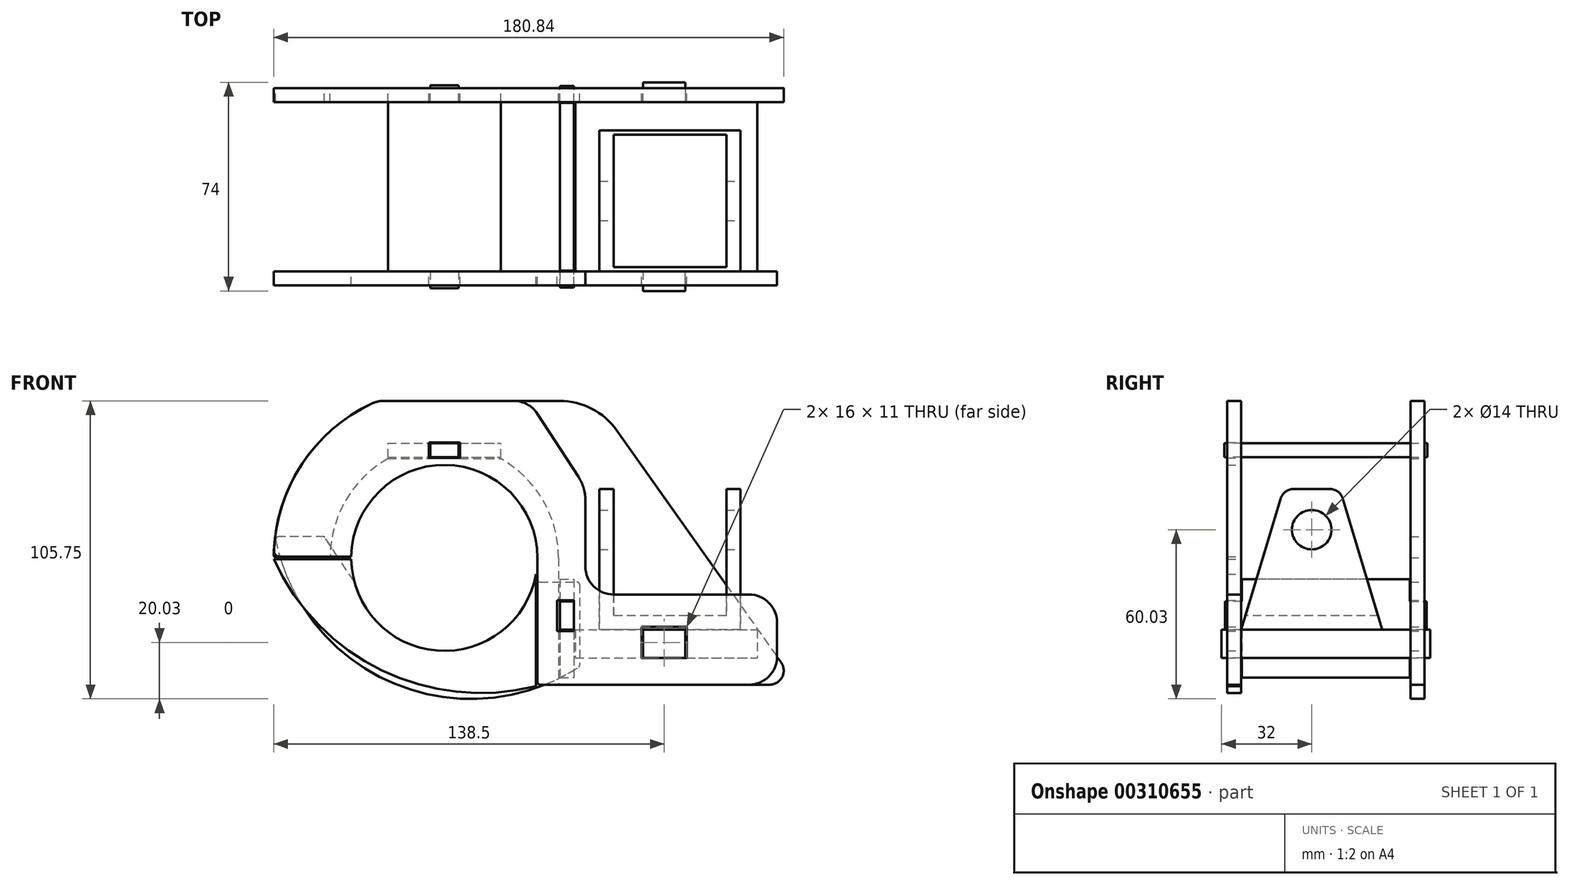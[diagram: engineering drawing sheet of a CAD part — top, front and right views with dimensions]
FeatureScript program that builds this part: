
annotation { "Feature Type Name" : "Feature", "Feature Type Description" : "" }
export const myFeature = defineFeature(function(context is Context, id is Id, definition is map)
    precondition{}
    {
        {
            var Q0;
            Q0=qCreatedBy(makeId("Front.planeOp"),FACE);
            var sketch = newSketch(context, id + "F0", { "sketchPlane" : qUnion([Q0])});
            skArc(sketch, "E0", {"start": v(40.5, 0) * mm, "mid": v(0, 40.5) * mm, "end": v(-40.5, 0) * mm, "construction": true});
            skLineSegment(sketch, "E1", {"start": v(-20, 35.22) * mm, "end": v(-5.5, 35.22) * mm});
            skLineSegment(sketch, "E2", {"start": v(-5.5, 35.22) * mm, "end": v(-5.5, 40.72) * mm});
            skLineSegment(sketch, "E3", {"start": v(-5.5, 40.72) * mm, "end": v(5.5, 40.72) * mm});
            skLineSegment(sketch, "E4", {"start": v(5.5, 40.72) * mm, "end": v(5.5, 35.22) * mm});
            skLineSegment(sketch, "E5", {"start": v(5.5, 35.22) * mm, "end": v(20, 35.22) * mm});
            skPoint(sketch, "E6", {"position": v(0, 40.72) * mm});
            skArc(sketch, "E7", {"start": v(-20, 35.22) * mm, "mid": v(-35, 20.37) * mm, "end": v(-40.5, 0) * mm});
            skArc(sketch, "E8", {"start": v(40.5, 0) * mm, "mid": v(35, 20.37) * mm, "end": v(20, 35.22) * mm});
            skArc(sketch, "E9.0", {"start": v(-25.7, 54.77) * mm, "mid": v(-50.79, 32.87) * mm, "end": v(-60.5, 1.02) * mm});
            skLineSegment(sketch, "E10", {"start": v(-59.5, 0) * mm, "end": v(-40.5, 0) * mm});
            skLineSegment(sketch, "E11", {"start": v(-21.45, 55.72) * mm, "end": v(40.81, 55.72) * mm});
            skLineSegment(sketch, "E12", {"start": v(40.5, 0) * mm, "end": v(40.5, -15) * mm});
            skLineSegment(sketch, "E13", {"start": v(40.5, -45) * mm, "end": v(115.34, -45) * mm});
            skArc(sketch, "E14", {"start": v(-32.5, 0) * mm, "mid": v(0, -32.5) * mm, "end": v(32.5, 0) * mm, "construction": true});
            skLineSegment(sketch, "E15", {"start": v(-40.5, 0) * mm, "end": v(-32.5, 0) * mm, "construction": true});
            skLineSegment(sketch, "E16", {"start": v(40.5, 0) * mm, "end": v(32.5, 0) * mm, "construction": true});
            skPoint(sketch, "E17", {"position": v(80, 10) * mm});
            skLineSegment(sketch, "E18", {"start": v(61.22, 45.15) * mm, "end": v(119.42, -37.11) * mm});
            skLineSegment(sketch, "E19.bottom", {"start": v(70, -24.5) * mm, "end": v(86, -24.5) * mm});
            skLineSegment(sketch, "E19.top", {"start": v(70, -35.5) * mm, "end": v(86, -35.5) * mm});
            skLineSegment(sketch, "E19.left", {"start": v(70, -24.5) * mm, "end": v(70, -35.5) * mm});
            skLineSegment(sketch, "E19.right", {"start": v(86, -24.5) * mm, "end": v(86, -35.5) * mm});
            skPoint(sketch, "E20.visualSharp", {"position": v(-23.58, 55.72) * mm});
            skArc(sketch, "E20.filletArc", {"start": v(-21.45, 55.72) * mm, "mid": v(-23.63, 55.48) * mm, "end": v(-25.7, 54.77) * mm});
            skPoint(sketch, "E21.visualSharp", {"position": v(53.75, 55.72) * mm});
            skArc(sketch, "E21.filletArc", {"start": v(61.22, 45.15) * mm, "mid": v(52.3, 52.92) * mm, "end": v(40.81, 55.72) * mm});
            skPoint(sketch, "E22.visualSharp", {"position": v(125, -45) * mm});
            skArc(sketch, "E22.filletArc", {"start": v(115.34, -45) * mm, "mid": v(119.78, -42.3) * mm, "end": v(119.42, -37.11) * mm});
            skLineSegment(sketch, "E23", {"start": v(40.5, -15) * mm, "end": v(46, -15) * mm});
            skLineSegment(sketch, "E24", {"start": v(46, -15) * mm, "end": v(46, -26) * mm});
            skLineSegment(sketch, "E25", {"start": v(46, -26) * mm, "end": v(40.5, -26) * mm});
            skLineSegment(sketch, "E26.trimOffspring", {"start": v(40.5, -26) * mm, "end": v(40.5, -45) * mm});
            skPoint(sketch, "E27.visualSharp", {"position": v(-60.5, 0) * mm});
            skArc(sketch, "E27.filletArc", {"start": v(-60.5, 1.02) * mm, "mid": v(-60.2, 0.3) * mm, "end": v(-59.5, 0) * mm});
            skSolve(sketch);
        }
        {
            var Q0;
            Q0 = qSketchRegion(id + "F0", true);
            var Q1;
            Q1 = qConstructionFilter(qBodyType(qCreatedBy(id + "F0" ,EDGE), BodyType.WIRE), ConstructionObject.NO);
            extrude(context, id + "F1", {"entities" : qUnion([Q0]), "surfaceEntities" : qUnion([Q1]), "depth" : 5 * mm});
        }
        {
            var Q0;
            Q0=qCreatedBy(makeId("Front.planeOp"),FACE);
            var sketch = newSketch(context, id + "F2", { "sketchPlane" : qUnion([Q0])});
            skArc(sketch, "E28", {"start": v(-31.77, -8.91) * mm, "mid": v(-0.7, -33) * mm, "end": v(31.36, -10.26) * mm});
            skLineSegment(sketch, "E29", {"start": v(-31.88, -8.54) * mm, "end": v(0, 0) * mm, "construction": true});
            skLineSegment(sketch, "E30", {"start": v(31.88, -8.54) * mm, "end": v(0, 0) * mm, "construction": true});
            skLineSegment(sketch, "E31", {"start": v(-32.1, -8.2) * mm, "end": v(-42.53, 7.5) * mm});
            skLineSegment(sketch, "E32", {"start": v(-42.53, 7.5) * mm, "end": v(-58.82, 7.5) * mm});
            skLineSegment(sketch, "E33", {"start": v(33.74, -8.54) * mm, "end": v(47, -8.54) * mm});
            skLineSegment(sketch, "E34", {"start": v(48, -9.54) * mm, "end": v(48, -38) * mm});
            skArc(sketch, "E35", {"start": v(-59.8, 6.3) * mm, "mid": v(-18, -44.51) * mm, "end": v(47.54, -38.84) * mm});
            skPoint(sketch, "E36.visualSharp", {"position": v(-31.88, -8.54) * mm});
            skArc(sketch, "E36.filletArc", {"start": v(-31.77, -8.91) * mm, "mid": v(-31.9, -8.55) * mm, "end": v(-32.1, -8.2) * mm});
            skPoint(sketch, "E37.visualSharp", {"position": v(31.88, -8.54) * mm});
            skArc(sketch, "E37.filletArc", {"start": v(33.74, -8.54) * mm, "mid": v(32.27, -9.02) * mm, "end": v(31.36, -10.26) * mm});
            skPoint(sketch, "E38.visualSharp", {"position": v(-60.03, 7.5) * mm});
            skArc(sketch, "E38.filletArc", {"start": v(-58.82, 7.5) * mm, "mid": v(-59.6, 7.13) * mm, "end": v(-59.8, 6.3) * mm});
            skPoint(sketch, "E39.visualSharp", {"position": v(48, -38.54) * mm});
            skArc(sketch, "E39.filletArc", {"start": v(47.54, -38.84) * mm, "mid": v(47.88, -38.48) * mm, "end": v(48, -38) * mm});
            skPoint(sketch, "E40.visualSharp", {"position": v(48, -8.54) * mm});
            skArc(sketch, "E40.filletArc", {"start": v(48, -9.54) * mm, "mid": v(47.7, -8.83) * mm, "end": v(47, -8.54) * mm});
            skSolve(sketch);
        }
        {
            var Q0;
            Q0 = qSketchRegion(id + "F2", true);
            extrude(context, id + "F3", {"entities" : qUnion([Q0]), "depth" : 5 * mm});
        }
        {
            var Q0;
            Q0=makeQuery(id+"F1.opExtrude","SWEPT_FACE",FACE,{"disambiguationData":[OSD([sQuery(id+"F0.wireOp",EDGE,"E19.top")])]});
            var sketch = newSketch(context, id + "F4", { "sketchPlane" : qUnion([Q0])});
            skLineSegment(sketch, "E41.bottom", {"start": v(46.5, -5) * mm, "end": v(111, -5) * mm});
            skLineSegment(sketch, "E41.top", {"start": v(46.5, -65) * mm, "end": v(111, -65) * mm});
            skLineSegment(sketch, "E41.left", {"start": v(46.5, -5) * mm, "end": v(46.5, -65) * mm});
            skLineSegment(sketch, "E41.right", {"start": v(111, -5) * mm, "end": v(111, -65) * mm});
            skLineSegment(sketch, "E42", {"start": v(70.5, -5) * mm, "end": v(70.5, 2) * mm});
            skLineSegment(sketch, "E43", {"start": v(70.5, 2) * mm, "end": v(85.5, 2) * mm});
            skLineSegment(sketch, "E44", {"start": v(85.5, 2) * mm, "end": v(85.5, -5) * mm});
            skLineSegment(sketch, "E45", {"start": v(70.5, -65) * mm, "end": v(70.5, -72) * mm});
            skLineSegment(sketch, "E46", {"start": v(70.5, -72) * mm, "end": v(85.5, -72) * mm});
            skLineSegment(sketch, "E47", {"start": v(85.5, -72) * mm, "end": v(85.5, -65) * mm});
            skSolve(sketch);
        }
        {
            var Q0;
            Q0 = qSketchRegion(id + "F4", true);
            extrude(context, id + "F5", {"entities" : qUnion([Q0]), "depth" : 10 * mm});
        }
        {
            var Q0;
            {var subQ0=sQuery(id+"F4.wireOp",EDGE,"E41.top");Q0=makeQuery(id+"F5.opExtrude","SWEPT_FACE",FACE,{"disambiguationData":[OSD([subQ0]),TDD([makeQuery(id+"F4.imprint","IMPRINT",EDGE,{"disambiguationData":[TD([[makeQuery(id+"F4.imprint","INTERSECT",VERTEX,{"derivedFrom":[subQ0,sQuery(id+"F4.wireOp",EDGE,"E41.left")]}),-1.0]])],"derivedFrom":subQ0})])]});}
            var sketch = newSketch(context, id + "F6", { "sketchPlane" : qUnion([Q0])});
            skLineSegment(sketch, "E48", {"start": v(60, 24.5) * mm, "end": v(60, -20.5) * mm});
            skLineSegment(sketch, "E49", {"start": v(60, -20.5) * mm, "end": v(100, -20.5) * mm});
            skLineSegment(sketch, "E50", {"start": v(100, -20.5) * mm, "end": v(100, 24.5) * mm});
            skLineSegment(sketch, "E51", {"start": v(100, 24.5) * mm, "end": v(105, 24.5) * mm});
            skLineSegment(sketch, "E52", {"start": v(105, 24.5) * mm, "end": v(105, -25.5) * mm});
            skLineSegment(sketch, "E53", {"start": v(105, -25.5) * mm, "end": v(55, -25.5) * mm});
            skLineSegment(sketch, "E54", {"start": v(55, -25.5) * mm, "end": v(55, 24.5) * mm});
            skLineSegment(sketch, "E55", {"start": v(55, 24.5) * mm, "end": v(60, 24.5) * mm});
            skSolve(sketch);
        }
        {
            var Q0;
            Q0 = qSketchRegion(id + "F6", true);
            extrude(context, id + "F7", {"entities" : qUnion([Q0]), "oppositeDirection" : true, "depth" : 50 * mm});
        }
        {
            var Q0;
            Q0=makeQuery(id+"F7.opExtrude","SWEPT_FACE",FACE,{"disambiguationData":[OSD([sQuery(id+"F6.wireOp",EDGE,"E52")])]});
            var sketch = newSketch(context, id + "F8", { "sketchPlane" : qUnion([Q0])});
            skCircle(sketch, "E56", {"center": v(-40, 10) * mm, "radius": 7 * mm});
            skLineSegment(sketch, "E57", {"start": v(-46.28, 24.5) * mm, "end": v(-33.72, 24.5) * mm});
            skPoint(sketch, "E58", {"position": v(-40, 24.5) * mm});
            skLineSegment(sketch, "E59", {"start": v(-65, -25.5) * mm, "end": v(-51.07, 20.94) * mm});
            skLineSegment(sketch, "E60", {"start": v(-28.93, 20.94) * mm, "end": v(-15, -25.5) * mm});
            skPoint(sketch, "E61.visualSharp", {"position": v(-50, 24.5) * mm});
            skArc(sketch, "E61.filletArc", {"start": v(-46.28, 24.5) * mm, "mid": v(-49.26, 23.51) * mm, "end": v(-51.07, 20.94) * mm});
            skPoint(sketch, "E62.visualSharp", {"position": v(-30, 24.5) * mm});
            skArc(sketch, "E62.filletArc", {"start": v(-28.93, 20.94) * mm, "mid": v(-30.74, 23.51) * mm, "end": v(-33.72, 24.5) * mm});
            skLineSegment(sketch, "E63", {"start": v(-46.28, 24.5) * mm, "end": v(-65, 24.5) * mm});
            skLineSegment(sketch, "E64", {"start": v(-65, 24.5) * mm, "end": v(-65, -25.5) * mm});
            skLineSegment(sketch, "E65", {"start": v(-33.72, 24.5) * mm, "end": v(-15, 24.5) * mm});
            skLineSegment(sketch, "E66", {"start": v(-15, 24.5) * mm, "end": v(-15, -25.5) * mm});
            skSolve(sketch);
        }
        {
            var Q0;
            Q0 = qSketchRegion(id + "F8", true);
            extrude(context, id + "F9", {"entities" : qUnion([Q0]), "operationType" : NewBodyOperationType.REMOVE, "oppositeDirection" : true, "depth" : 602 * mm});
        }
        {
            var Q0;
            {var subQ0=sQuery(id+"F4.wireOp",EDGE,"E41.top");Q0=makeQuery(id+"F5.opExtrude","SWEPT_FACE",FACE,{"disambiguationData":[OSD([subQ0]),TDD([makeQuery(id+"F4.imprint","IMPRINT",EDGE,{"disambiguationData":[TD([[makeQuery(id+"F4.imprint","INTERSECT",VERTEX,{"derivedFrom":[subQ0,sQuery(id+"F4.wireOp",EDGE,"E41.right")]}),1.0]])],"derivedFrom":subQ0})])]});}
            var sketch = newSketch(context, id + "F10", { "sketchPlane" : qUnion([Q0])});
            skArc(sketch, "E67", {"start": v(33, 0) * mm, "mid": v(0.25, 33) * mm, "end": v(-33, 0.5) * mm});
            skLineSegment(sketch, "E68", {"start": v(-33, 0.5) * mm, "end": v(-58.44, 0.5) * mm});
            skArc(sketch, "E69", {"start": v(-25.7, 54.77) * mm, "mid": v(-50.36, 33.53) * mm, "end": v(-60.44, 2.59) * mm});
            skLineSegment(sketch, "E70", {"start": v(-21.45, 55.72) * mm, "end": v(24.58, 55.72) * mm});
            skPoint(sketch, "E71.orphan", {"position": v(0, 60.5) * mm});
            skLineSegment(sketch, "E72", {"start": v(50, 20.55) * mm, "end": v(50, 0.02) * mm});
            skLineSegment(sketch, "E73", {"start": v(33, 0) * mm, "end": v(33, -44) * mm});
            skLineSegment(sketch, "E74", {"start": v(34, -45) * mm, "end": v(108, -45) * mm});
            skLineSegment(sketch, "E75", {"start": v(118, -35) * mm, "end": v(118, -23) * mm});
            skLineSegment(sketch, "E76", {"start": v(108, -13) * mm, "end": v(60, -13) * mm});
            skLineSegment(sketch, "E77", {"start": v(50, -3) * mm, "end": v(50, 0.02) * mm});
            skLineSegment(sketch, "E78.bottom", {"start": v(70, -24.5) * mm, "end": v(86, -24.5) * mm});
            skLineSegment(sketch, "E78.top", {"start": v(70, -35.5) * mm, "end": v(86, -35.5) * mm});
            skLineSegment(sketch, "E78.left", {"start": v(70, -24.5) * mm, "end": v(70, -35.5) * mm});
            skLineSegment(sketch, "E78.right", {"start": v(86, -24.5) * mm, "end": v(86, -35.5) * mm});
            skPoint(sketch, "E79.visualSharp", {"position": v(-23.57, 55.72) * mm});
            skArc(sketch, "E79.filletArc", {"start": v(-21.45, 55.72) * mm, "mid": v(-23.62, 55.48) * mm, "end": v(-25.7, 54.77) * mm});
            skPoint(sketch, "E80.visualSharp", {"position": v(-60.5, 0.5) * mm});
            skArc(sketch, "E80.filletArc", {"start": v(-60.44, 2.59) * mm, "mid": v(-59.89, 1.12) * mm, "end": v(-58.44, 0.5) * mm});
            skPoint(sketch, "E81.visualSharp", {"position": v(50, 55.72) * mm});
            skPoint(sketch, "E82.visualSharp", {"position": v(50, -13) * mm});
            skArc(sketch, "E82.filletArc", {"start": v(50, -3) * mm, "mid": v(52.93, -10.07) * mm, "end": v(60, -13) * mm});
            skPoint(sketch, "E83.visualSharp", {"position": v(33, -45) * mm});
            skArc(sketch, "E83.filletArc", {"start": v(33, -44) * mm, "mid": v(33.3, -44.7) * mm, "end": v(34, -45) * mm});
            skPoint(sketch, "E84.visualSharp", {"position": v(118, -45) * mm});
            skArc(sketch, "E84.filletArc", {"start": v(108, -45) * mm, "mid": v(115.07, -42.07) * mm, "end": v(118, -35) * mm});
            skPoint(sketch, "E85.visualSharp", {"position": v(118, -13) * mm});
            skArc(sketch, "E85.filletArc", {"start": v(118, -23) * mm, "mid": v(115.07, -15.93) * mm, "end": v(108, -13) * mm});
            skLineSegment(sketch, "E86", {"start": v(32.96, 51.17) * mm, "end": v(47.57, 28.73) * mm});
            skPoint(sketch, "E87.visualSharp", {"position": v(50, 25) * mm});
            skArc(sketch, "E87.filletArc", {"start": v(50, 20.55) * mm, "mid": v(49.38, 24.82) * mm, "end": v(47.57, 28.73) * mm});
            skPoint(sketch, "E88.visualSharp", {"position": v(30, 55.72) * mm});
            skArc(sketch, "E88.filletArc", {"start": v(32.96, 51.17) * mm, "mid": v(29.34, 54.5) * mm, "end": v(24.58, 55.72) * mm});
            skArc(sketch, "E89", {"start": v(-33, -0.5) * mm, "mid": v(-2.62, -32.9) * mm, "end": v(32.5, -5.72) * mm});
            skLineSegment(sketch, "E90", {"start": v(32.5, -5.72) * mm, "end": v(32.5, -45.5) * mm});
            skLineSegment(sketch, "E91", {"start": v(-60.5, -0.5) * mm, "end": v(-33, -0.5) * mm});
            skArc(sketch, "E92", {"start": v(-60.5, -0.5) * mm, "mid": v(-22.18, -39.92) * mm, "end": v(32.5, -45.5) * mm});
            skLineSegment(sketch, "E93.bottom", {"start": v(-5.5, 35.5) * mm, "end": v(5.5, 35.5) * mm});
            skLineSegment(sketch, "E93.top", {"start": v(-5.5, 41) * mm, "end": v(5.5, 41) * mm});
            skLineSegment(sketch, "E93.left", {"start": v(-5.5, 35.5) * mm, "end": v(-5.5, 41) * mm});
            skLineSegment(sketch, "E93.right", {"start": v(5.5, 35.5) * mm, "end": v(5.5, 41) * mm});
            skPoint(sketch, "E94", {"position": v(0, 35.5) * mm});
            skLineSegment(sketch, "E95.bottom", {"start": v(40, -15) * mm, "end": v(46, -15) * mm});
            skLineSegment(sketch, "E95.top", {"start": v(40, -26) * mm, "end": v(46, -26) * mm});
            skLineSegment(sketch, "E95.left", {"start": v(40, -15) * mm, "end": v(40, -26) * mm});
            skLineSegment(sketch, "E95.right", {"start": v(46, -15) * mm, "end": v(46, -26) * mm});
            skSolve(sketch);
        }
        {
            var Q0;
            Q0 = qSketchRegion(id + "F10", true);
            extrude(context, id + "F11", {"entities" : qUnion([Q0]), "depth" : 5 * mm});
        }
        {
            var Q0;
            Q0=makeQuery(id+"F1.opExtrude","SWEPT_FACE",FACE,{"disambiguationData":[OSD([sQuery(id+"F0.wireOp",EDGE,"E3")])]});
            var sketch = newSketch(context, id + "F12", { "sketchPlane" : qUnion([Q0])});
            skLineSegment(sketch, "E96.bottom", {"start": v(-20, 5) * mm, "end": v(20, 5) * mm});
            skLineSegment(sketch, "E96.top", {"start": v(-20, 65) * mm, "end": v(20, 65) * mm});
            skLineSegment(sketch, "E96.left", {"start": v(-20, 5) * mm, "end": v(-20, 65) * mm});
            skLineSegment(sketch, "E96.right", {"start": v(20, 5) * mm, "end": v(20, 65) * mm});
            skLineSegment(sketch, "E97.bottom", {"start": v(-5, 5) * mm, "end": v(5, 5) * mm});
            skLineSegment(sketch, "E97.top", {"start": v(-5, -1) * mm, "end": v(5, -1) * mm});
            skLineSegment(sketch, "E97.left", {"start": v(-5, 5) * mm, "end": v(-5, -1) * mm});
            skLineSegment(sketch, "E97.right", {"start": v(5, 5) * mm, "end": v(5, -1) * mm});
            skLineSegment(sketch, "E98.bottom", {"start": v(-5, 65) * mm, "end": v(5, 65) * mm});
            skLineSegment(sketch, "E98.top", {"start": v(-5, 71) * mm, "end": v(5, 71) * mm});
            skLineSegment(sketch, "E98.left", {"start": v(-5, 65) * mm, "end": v(-5, 71) * mm});
            skLineSegment(sketch, "E98.right", {"start": v(5, 65) * mm, "end": v(5, 71) * mm});
            skSolve(sketch);
        }
        {
            var Q0;
            Q0 = qSketchRegion(id + "F12", true);
            extrude(context, id + "F13", {"entities" : qUnion([Q0]), "depth" : 5 * mm});
        }
        {
            var Q0;
            Q0=makeQuery(id+"F1.opExtrude","SWEPT_FACE",FACE,{"disambiguationData":[OSD([sQuery(id+"F0.wireOp",EDGE,"E24")])]});
            var sketch = newSketch(context, id + "F14", { "sketchPlane" : qUnion([Q0])});
            skLineSegment(sketch, "E99.bottom", {"start": v(5.25, -7.5) * mm, "end": v(64.75, -7.5) * mm});
            skLineSegment(sketch, "E99.top", {"start": v(5.25, -42.5) * mm, "end": v(64.75, -42.5) * mm});
            skLineSegment(sketch, "E99.left", {"start": v(5.25, -7.5) * mm, "end": v(5.25, -42.5) * mm});
            skLineSegment(sketch, "E99.right", {"start": v(64.75, -7.5) * mm, "end": v(64.75, -42.5) * mm});
            skLineSegment(sketch, "E100.bottom", {"start": v(5.25, -15.5) * mm, "end": v(-0.75, -15.5) * mm});
            skLineSegment(sketch, "E100.top", {"start": v(5.25, -25.5) * mm, "end": v(-0.75, -25.5) * mm});
            skLineSegment(sketch, "E100.left", {"start": v(5.25, -15.5) * mm, "end": v(5.25, -25.5) * mm});
            skLineSegment(sketch, "E100.right", {"start": v(-0.75, -15.5) * mm, "end": v(-0.75, -25.5) * mm});
            skLineSegment(sketch, "E101.bottom", {"start": v(64.75, -15.5) * mm, "end": v(70.75, -15.5) * mm});
            skLineSegment(sketch, "E101.left", {"start": v(64.75, -15.5) * mm, "end": v(64.75, -26) * mm});
            skLineSegment(sketch, "E101.right", {"start": v(70.75, -15.5) * mm, "end": v(70.75, -25.5) * mm});
            skLineSegment(sketch, "E102", {"start": v(70.75, -25.5) * mm, "end": v(64.75, -25.5) * mm});
            skSolve(sketch);
        }
        {
            var Q0;
            Q0 = qSketchRegion(id + "F14", true);
            extrude(context, id + "F15", {"entities" : qUnion([Q0]), "depth" : 5 * mm});
        }
    });
